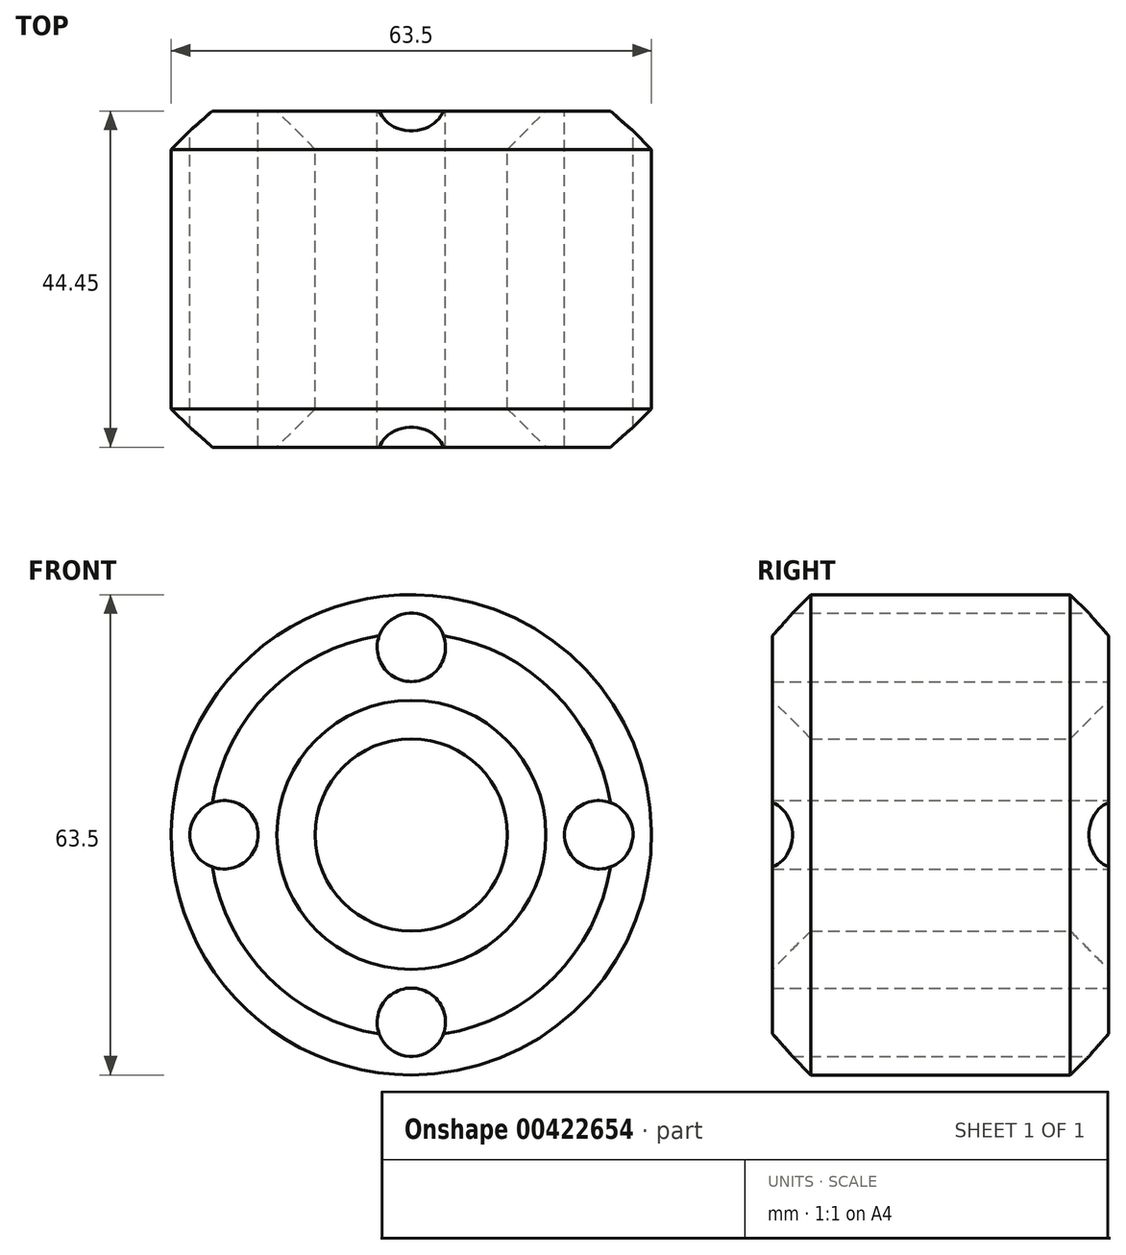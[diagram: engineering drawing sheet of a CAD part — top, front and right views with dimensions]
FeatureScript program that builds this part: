
annotation { "Feature Type Name" : "Feature", "Feature Type Description" : "" }
export const myFeature = defineFeature(function(context is Context, id is Id, definition is map)
    precondition{}
    {
        {
            var Q0;
            Q0=qCreatedBy(makeId("Front.planeOp"),FACE);
            var sketch = newSketch(context, id + "F0", { "sketchPlane" : qUnion([Q0])});
            skCircle(sketch, "E0", {"center": v(0, 0) * mm, "radius": 31.75 * mm});
            skCircle(sketch, "E1", {"center": v(0, 0) * mm, "radius": 12.7 * mm});
            skCircle(sketch, "E2", {"center": v(0, 0) * mm, "radius": 19.2 * mm});
            skCircle(sketch, "E3", {"center": v(0, 0) * mm, "radius": 24.78 * mm});
            skPoint(sketch, "E4", {"position": v(0, 24.78) * mm});
            skPoint(sketch, "E5", {"position": v(0, -24.78) * mm});
            skPoint(sketch, "E6", {"position": v(24.78, 0) * mm});
            skPoint(sketch, "E7", {"position": v(-24.78, 0) * mm});
            skSolve(sketch);
        }
        {
            var Q0;
            Q0=makeQuery(id+"F0.imprint","IMPRINT",FACE,{"disambiguationData":[TD([[makeQuery(id+"F0.imprint","IMPRINT",EDGE,{"derivedFrom":sQuery(id+"F0.wireOp",EDGE,"E1")}),-1.0]])]});
            var Q1;
            Q1=makeQuery(id+"F0.imprint","IMPRINT",FACE,{"disambiguationData":[TD([[makeQuery(id+"F0.imprint","IMPRINT",EDGE,{"derivedFrom":sQuery(id+"F0.wireOp",EDGE,"E2")}),-1.0]])]});
            var Q2;
            Q2=makeQuery(id+"F0.imprint","IMPRINT",FACE,{"disambiguationData":[TD([[makeQuery(id+"F0.imprint","IMPRINT",EDGE,{"derivedFrom":sQuery(id+"F0.wireOp",EDGE,"E0")}),1.0]])]});
            extrude(context, id + "F1", {"entities" : qUnion([Q0, Q1, Q2]), "depth" : 44.45 * mm});
        }
        {
            var Q0;
            Q0=sQuery(id+"F0.wireOp",VERTEX,"E6");
            var Q1;
            Q1=sQuery(id+"F0.wireOp",VERTEX,"E5");
            var Q2;
            Q2=sQuery(id+"F0.wireOp",VERTEX,"E7");
            var Q3;
            Q3=sQuery(id+"F0.wireOp",VERTEX,"E4");
            var Q4;
            Q4=makeQuery(id+"F1.opExtrude","SWEPT_BODY",BODY,{"disambiguationData":[OSD([sQuery(id+"F0.wireOp",EDGE,"E0"),sQuery(id+"F0.wireOp",EDGE,"E1")])]});
            hole(context, id + "F2", {"style" : HoleStyle.SIMPLE, "endStyle" : HoleEndStyle.THROUGH, "oppositeDirection" : true, "holeDiameter" : 9.04 * mm, "isTappedThrough" : true, "tappedDepth" : 12.7 * mm, "tapClearance" : 3, "locations" : qUnion([Q0, Q1, Q2, Q3]), "scope" : qUnion([Q4])});
        }
        {
            var Q0;
            Q0=makeQuery(id+"F1.opExtrude","CAP_EDGE",EDGE,{"disambiguationData":[OSD([sQuery(id+"F0.wireOp",EDGE,"E1")])],"isStart":false});
            var Q1;
            Q1=makeQuery(id+"F1.opExtrude","CAP_EDGE",EDGE,{"disambiguationData":[OSD([sQuery(id+"F0.wireOp",EDGE,"E0")])],"isStart":false});
            var Q2;
            Q2=makeQuery(id+"F1.opExtrude","CAP_EDGE",EDGE,{"disambiguationData":[OSD([sQuery(id+"F0.wireOp",EDGE,"E1")])],"isStart":true});
            var Q3;
            Q3=makeQuery(id+"F1.opExtrude","CAP_EDGE",EDGE,{"disambiguationData":[OSD([sQuery(id+"F0.wireOp",EDGE,"E0")])],"isStart":true});
            chamfer(context, id + "F3", {"entities" : qUnion([Q0, Q1, Q2, Q3]), "width" : 5.08 * mm, "tangentPropagation" : true});
        }
    });
